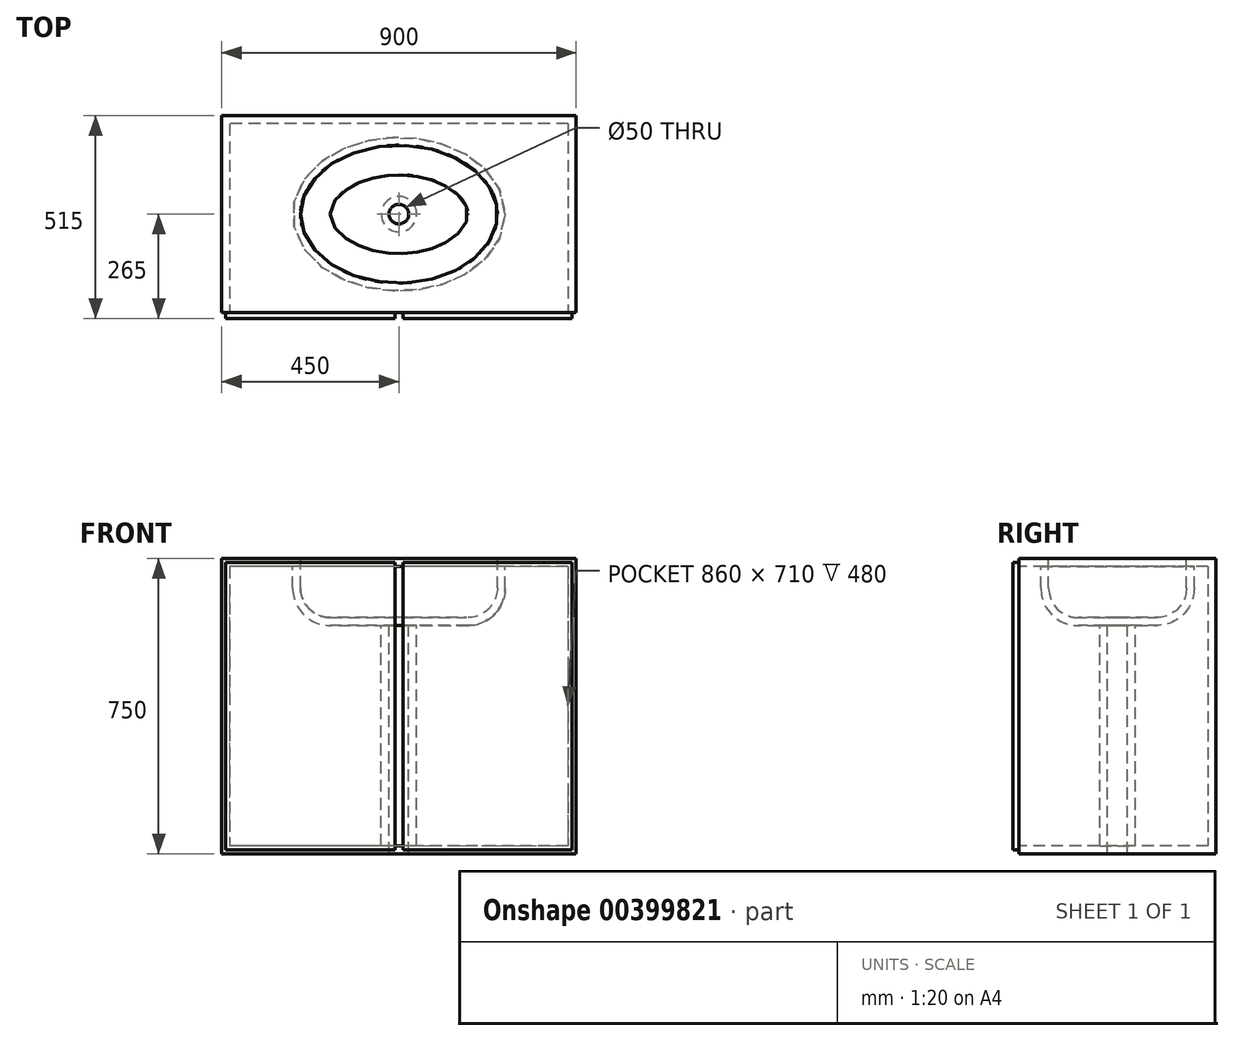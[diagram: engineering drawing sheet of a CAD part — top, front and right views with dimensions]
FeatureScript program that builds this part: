
annotation { "Feature Type Name" : "Feature", "Feature Type Description" : "" }
export const myFeature = defineFeature(function(context is Context, id is Id, definition is map)
    precondition{}
    {
        {
            var Q0;
            Q0=qCreatedBy(makeId("Top.planeOp"),FACE);
            var sketch = newSketch(context, id + "F0", { "sketchPlane" : qUnion([Q0])});
            skLineSegment(sketch, "E0.bottom", {"start": v(450, 250) * mm, "end": v(-450, 250) * mm});
            skLineSegment(sketch, "E0.top", {"start": v(450, -250) * mm, "end": v(-450, -250) * mm});
            skLineSegment(sketch, "E0.left", {"start": v(450, 250) * mm, "end": v(450, -250) * mm});
            skLineSegment(sketch, "E0.right", {"start": v(-450, 250) * mm, "end": v(-450, -250) * mm});
            skPoint(sketch, "E0.middle", {"position": v(0, 0) * mm});
            skSolve(sketch);
        }
        {
            var Q0;
            Q0 = qSketchRegion(id + "F0", true);
            extrude(context, id + "F1", {"entities" : qUnion([Q0]), "depth" : 750 * mm});
        }
        {
            var Q0;
            Q0=makeQuery(id+"F1.opExtrude","CAP_FACE",FACE,{"disambiguationData":[OSD([sQuery(id+"F0.wireOp",EDGE,"E0.bottom"),sQuery(id+"F0.wireOp",EDGE,"E0.top"),sQuery(id+"F0.wireOp",EDGE,"E0.left"),sQuery(id+"F0.wireOp",EDGE,"E0.right")])],"isStart":false});
            var sketch = newSketch(context, id + "F2", { "sketchPlane" : qUnion([Q0])});
            skEllipse(sketch, "E1", {"center": v(0, 0) * mm, "majorRadius": 175 * mm, "minorRadius": 250 * mm, "majorAxis": v(0, 1)});
            skSolve(sketch);
        }
        {
            var Q0;
            Q0 = qSketchRegion(id + "F2", true);
            extrude(context, id + "F3", {"entities" : qUnion([Q0]), "operationType" : NewBodyOperationType.REMOVE, "oppositeDirection" : true, "depth" : 150 * mm});
        }
        {
            var Q0;
            Q0=makeQuery(id+"F3.boolean.opBoolean","COPY",EDGE,{"derivedFrom":makeQuery(id+"F3.opExtrude","CAP_EDGE",EDGE,{"disambiguationData":[OSD([sQuery(id+"F2.wireOp",EDGE,"E1")])],"isStart":false})});
            fillet(context, id + "F4", {"entities" : qUnion([Q0]), "radius" : 75 * mm, "tangentPropagation" : true, "allowEdgeOverflow" : false});
        }
        {
            var Q0;
            Q0=makeQuery(id+"F3.boolean.opBoolean","COPY",FACE,{"derivedFrom":makeQuery(id+"F3.opExtrude","CAP_FACE",FACE,{"disambiguationData":[OSD([sQuery(id+"F2.wireOp",EDGE,"E1")])],"isStart":false})});
            var sketch = newSketch(context, id + "F5", { "sketchPlane" : qUnion([Q0])});
            skCircle(sketch, "E2", {"center": v(0, 0) * mm, "radius": 25 * mm});
            skSolve(sketch);
        }
        {
            var Q0;
            Q0 = qSketchRegion(id + "F5", true);
            extrude(context, id + "F6", {"entities" : qUnion([Q0]), "operationType" : NewBodyOperationType.REMOVE, "endBound" : BoundingType.THROUGH_ALL, "oppositeDirection" : true, "depth" : 25 * mm});
        }
        {
            var Q0;
            Q0=makeQuery(id+"F1.opExtrude","SWEPT_FACE",FACE,{"disambiguationData":[OSD([sQuery(id+"F0.wireOp",EDGE,"E0.top")])]});
            shell(context, id + "F7", {"entities" : qUnion([Q0]), "thickness" : 20 * mm});
        }
        {
            var Q0;
            Q0=makeQuery(id+"F1.opExtrude","SWEPT_FACE",FACE,{"disambiguationData":[OSD([sQuery(id+"F0.wireOp",EDGE,"E0.top")])]});
            var sketch = newSketch(context, id + "F8", { "sketchPlane" : qUnion([Q0])});
            skLineSegment(sketch, "E3.bottom", {"start": v(-440, 740) * mm, "end": v(-10, 740) * mm});
            skLineSegment(sketch, "E3.top", {"start": v(-440, 10) * mm, "end": v(-10, 10) * mm});
            skLineSegment(sketch, "E3.left", {"start": v(-440, 740) * mm, "end": v(-440, 10) * mm});
            skLineSegment(sketch, "E3.right", {"start": v(-10, 740) * mm, "end": v(-10, 10) * mm});
            skLineSegment(sketch, "E4.bottom", {"start": v(440, 740) * mm, "end": v(10, 740) * mm});
            skLineSegment(sketch, "E4.top", {"start": v(440, 10) * mm, "end": v(10, 10) * mm});
            skLineSegment(sketch, "E4.left", {"start": v(440, 740) * mm, "end": v(440, 10) * mm});
            skLineSegment(sketch, "E4.right", {"start": v(10, 740) * mm, "end": v(10, 10) * mm});
            skSolve(sketch);
        }
        {
            var Q0;
            Q0 = qSketchRegion(id + "F8", true);
            extrude(context, id + "F9", {"entities" : qUnion([Q0]), "depth" : 15 * mm});
        }
    });
